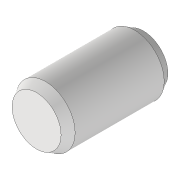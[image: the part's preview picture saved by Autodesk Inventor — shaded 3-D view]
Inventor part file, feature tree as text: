
AUTODESK INVENTOR PART (.ipt)
format: ipt  version: 2020 (Build 240168000, 168)  size: 97,280 bytes
history: native  units: mm
features: extrude x3, sketch x3
ambient origin geometry x8: Origin, YZ Plane, XZ Plane, XY Plane, X Axis, Y Axis, Z Axis, Center Point
bodies: Volumenkörper1 (feature_tree)
feature tree (6):
  extrude  "Extrusion1"  Depth=20.0mm TaperAngle=30.0deg
  extrude  "Extrusion2"  Depth=20.0mm
  extrude  "Extrusion3"  [1 undecoded]
  sketch  "Skizze1"  dims[d0=110.0mm d1=20.0mm d2=30.0deg]
  sketch  "Skizze2"  dims[d3=200.0mm d4=0.0mm d5=20.0mm d6=-5.235988mm]
  sketch  "Skizze3"
note: 1 required parameter value undecoded (feature->parameter linkage not recoverable at this tier; creation-order binding heuristic only, values carry confidence <= 0.55)
